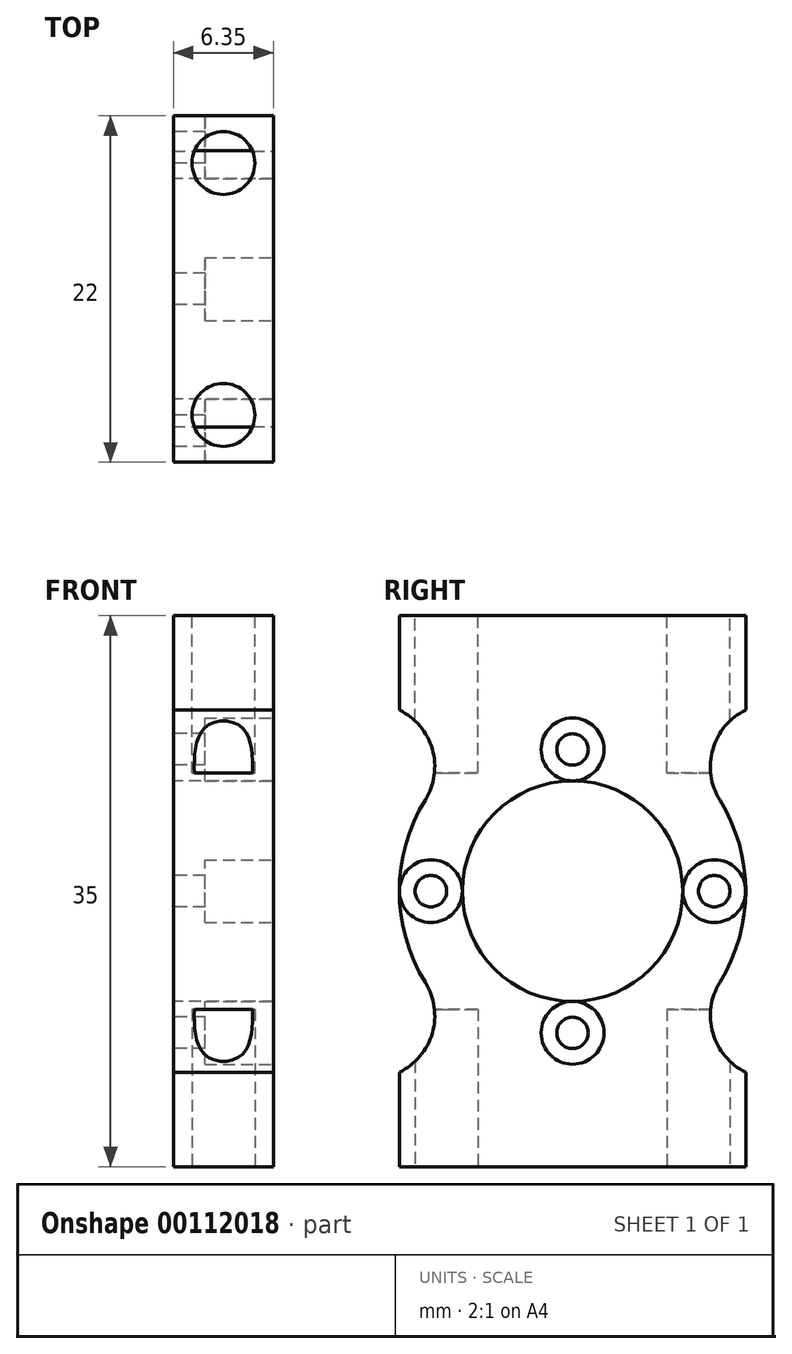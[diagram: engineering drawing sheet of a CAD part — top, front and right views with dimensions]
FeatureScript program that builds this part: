
annotation { "Feature Type Name" : "Feature", "Feature Type Description" : "" }
export const myFeature = defineFeature(function(context is Context, id is Id, definition is map)
    precondition{}
    {
        {
            var Q0;
            Q0=qCreatedBy(makeId("Right.planeOp"),FACE);
            var sketch = newSketch(context, id + "F0", { "sketchPlane" : qUnion([Q0])});
            skCircle(sketch, "E0", {"center": v(0, 0) * mm, "radius": 7 * mm});
            skArc(sketch, "E1", {"start": v(-6.42, 8.93) * mm, "mid": v(-11, 0) * mm, "end": v(-6.42, -8.93) * mm});
            skLineSegment(sketch, "E2", {"start": v(-11, 17.5) * mm, "end": v(11, 17.5) * mm});
            skLineSegment(sketch, "E3", {"start": v(-11, -17.5) * mm, "end": v(11, -17.5) * mm});
            skLineSegment(sketch, "E4", {"start": v(11, -17.5) * mm, "end": v(11, -11.5) * mm});
            skLineSegment(sketch, "E5", {"start": v(-11, -17.5) * mm, "end": v(-11, -11.5) * mm});
            skLineSegment(sketch, "E6", {"start": v(-11, 17.5) * mm, "end": v(-11, 11.5) * mm});
            skLineSegment(sketch, "E7", {"start": v(11, 17.5) * mm, "end": v(11, 11.5) * mm});
            skCircle(sketch, "E8", {"center": v(0, 0) * mm, "radius": 9 * mm, "construction": true});
            skCircle(sketch, "E9", {"center": v(0, 9) * mm, "radius": 1 * mm});
            skCircle(sketch, "E10", {"center": v(9, 0) * mm, "radius": 1 * mm});
            skCircle(sketch, "E11", {"center": v(0, -9) * mm, "radius": 1 * mm});
            skCircle(sketch, "E12", {"center": v(-9, 0) * mm, "radius": 1 * mm});
            skArc(sketch, "E13", {"start": v(-11, -11.5) * mm, "mid": v(-8.57, -10.47) * mm, "end": v(-6.42, -8.93) * mm});
            skArc(sketch, "E14", {"start": v(11, 11.5) * mm, "mid": v(8.57, 10.47) * mm, "end": v(6.42, 8.93) * mm});
            skLineSegment(sketch, "E15", {"start": v(-11, 17.5) * mm, "end": v(11, -17.5) * mm, "construction": true});
            skArc(sketch, "E16.trimOffspring", {"start": v(-6.42, 8.93) * mm, "mid": v(-8.57, 10.47) * mm, "end": v(-11, 11.5) * mm});
            skArc(sketch, "E17.trimOffspring", {"start": v(6.42, -8.93) * mm, "mid": v(8.57, -10.47) * mm, "end": v(11, -11.5) * mm});
            skArc(sketch, "E18.trimOffspring", {"start": v(6.42, -8.93) * mm, "mid": v(11, 0) * mm, "end": v(6.42, 8.93) * mm});
            skSolve(sketch);
        }
        {
            var Q0;
            Q0 = qSketchRegion(id + "F0", true);
            extrude(context, id + "F1", {"entities" : qUnion([Q0]), "depth" : 6.35 * mm});
        }
        {
            var Q0;
            Q0=makeQuery(id+"F1.opExtrude","SWEPT_EDGE",EDGE,{"disambiguationData":[OSD([sQuery(id+"F0.wireOp",EDGE,"E1"),sQuery(id+"F0.wireOp",EDGE,"E16.trimOffspring")])]});
            var Q1;
            Q1=makeQuery(id+"F1.opExtrude","SWEPT_EDGE",EDGE,{"disambiguationData":[OSD([sQuery(id+"F0.wireOp",EDGE,"E1"),sQuery(id+"F0.wireOp",EDGE,"E13")])]});
            var Q2;
            Q2=makeQuery(id+"F1.opExtrude","SWEPT_EDGE",EDGE,{"disambiguationData":[OSD([sQuery(id+"F0.wireOp",EDGE,"E17.trimOffspring"),sQuery(id+"F0.wireOp",EDGE,"E18.trimOffspring")])]});
            var Q3;
            Q3=makeQuery(id+"F1.opExtrude","SWEPT_EDGE",EDGE,{"disambiguationData":[OSD([sQuery(id+"F0.wireOp",EDGE,"E14"),sQuery(id+"F0.wireOp",EDGE,"E18.trimOffspring")])]});
            fillet(context, id + "F2", {"entities" : qUnion([Q0, Q1, Q2, Q3]), "radius" : 4 * mm, "tangentPropagation" : true, "allowEdgeOverflow" : false});
        }
        {
            var Q0;
            Q0=makeQuery(id+"F1.opExtrude","CAP_FACE",FACE,{"disambiguationData":[OSD([sQuery(id+"F0.wireOp",EDGE,"E0"),sQuery(id+"F0.wireOp",EDGE,"E1"),sQuery(id+"F0.wireOp",EDGE,"E2"),sQuery(id+"F0.wireOp",EDGE,"E3"),sQuery(id+"F0.wireOp",EDGE,"E4"),sQuery(id+"F0.wireOp",EDGE,"E5"),sQuery(id+"F0.wireOp",EDGE,"E6"),sQuery(id+"F0.wireOp",EDGE,"E7"),sQuery(id+"F0.wireOp",EDGE,"E9"),sQuery(id+"F0.wireOp",EDGE,"E10"),sQuery(id+"F0.wireOp",EDGE,"E11"),sQuery(id+"F0.wireOp",EDGE,"E12"),sQuery(id+"F0.wireOp",EDGE,"E13"),sQuery(id+"F0.wireOp",EDGE,"E14"),sQuery(id+"F0.wireOp",EDGE,"E16.trimOffspring"),sQuery(id+"F0.wireOp",EDGE,"E17.trimOffspring"),sQuery(id+"F0.wireOp",EDGE,"E18.trimOffspring")])],"isStart":false});
            var sketch = newSketch(context, id + "F3", { "sketchPlane" : qUnion([Q0])});
            skCircle(sketch, "E19", {"center": v(0, 9) * mm, "radius": 2 * mm});
            skCircle(sketch, "E20", {"center": v(9, 0) * mm, "radius": 2 * mm});
            skCircle(sketch, "E21", {"center": v(0, -9) * mm, "radius": 2 * mm});
            skCircle(sketch, "E22", {"center": v(-9, 0) * mm, "radius": 2 * mm});
            skSolve(sketch);
        }
        {
            var Q0;
            Q0 = qSketchRegion(id + "F3", true);
            extrude(context, id + "F4", {"entities" : qUnion([Q0]), "operationType" : NewBodyOperationType.REMOVE, "oppositeDirection" : true, "depth" : 4.35 * mm});
        }
        {
            var Q0;
            Q0=makeQuery(id+"F1.opExtrude","SWEPT_FACE",FACE,{"disambiguationData":[OSD([sQuery(id+"F0.wireOp",EDGE,"E2")])]});
            var sketch = newSketch(context, id + "F5", { "sketchPlane" : qUnion([Q0])});
            skCircle(sketch, "E23", {"center": v(3.17, 8) * mm, "radius": 2 * mm});
            skCircle(sketch, "E24", {"center": v(3.17, -8) * mm, "radius": 2 * mm});
            skLineSegment(sketch, "E25", {"start": v(3.17, 11) * mm, "end": v(3.17, 8) * mm, "construction": true});
            skLineSegment(sketch, "E26", {"start": v(3.17, -8) * mm, "end": v(3.18, -11) * mm, "construction": true});
            skSolve(sketch);
        }
        {
            var Q0;
            Q0 = qSketchRegion(id + "F5", true);
            extrude(context, id + "F6", {"entities" : qUnion([Q0]), "operationType" : NewBodyOperationType.REMOVE, "oppositeDirection" : true, "depth" : 10 * mm});
        }
        {
            var Q0;
            Q0=makeQuery(id+"F1.opExtrude","SWEPT_FACE",FACE,{"disambiguationData":[OSD([sQuery(id+"F0.wireOp",EDGE,"E3")])]});
            var sketch = newSketch(context, id + "F7", { "sketchPlane" : qUnion([Q0])});
            skCircle(sketch, "E27", {"center": v(3.17, 8) * mm, "radius": 2 * mm});
            skCircle(sketch, "E28", {"center": v(3.17, -8) * mm, "radius": 2 * mm});
            skLineSegment(sketch, "E29", {"start": v(3.18, 11) * mm, "end": v(3.18, 8) * mm, "construction": true});
            skLineSegment(sketch, "E30", {"start": v(3.17, -11) * mm, "end": v(3.17, -8) * mm, "construction": true});
            skSolve(sketch);
        }
        {
            var Q0;
            Q0 = qSketchRegion(id + "F7", true);
            extrude(context, id + "F8", {"entities" : qUnion([Q0]), "operationType" : NewBodyOperationType.REMOVE, "oppositeDirection" : true, "depth" : 10 * mm});
        }
    });
